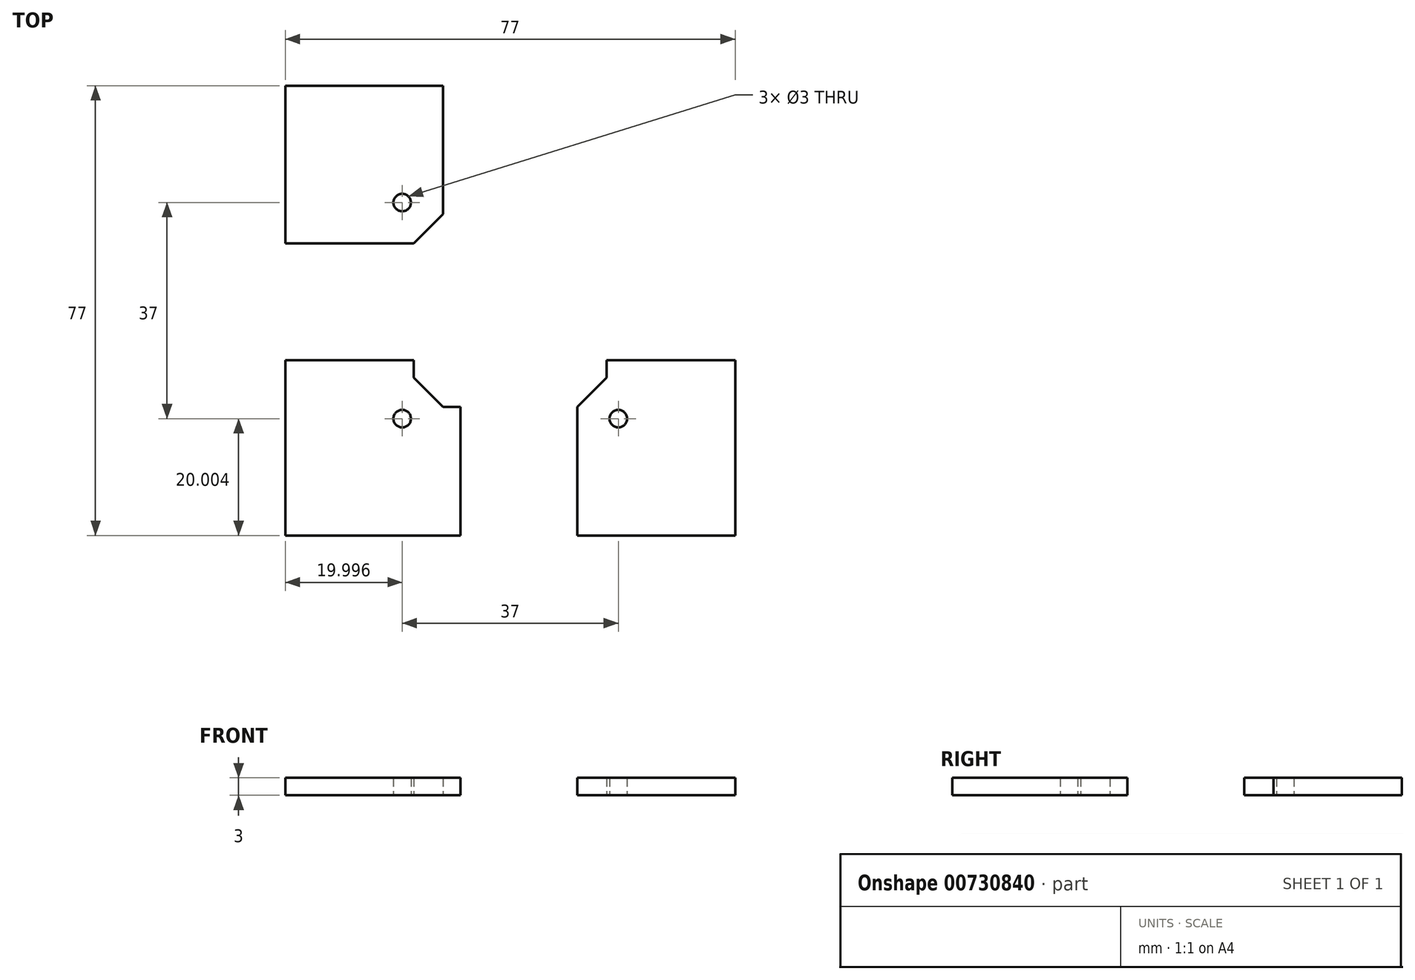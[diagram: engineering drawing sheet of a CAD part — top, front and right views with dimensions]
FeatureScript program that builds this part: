
annotation { "Feature Type Name" : "Feature", "Feature Type Description" : "" }
export const myFeature = defineFeature(function(context is Context, id is Id, definition is map)
    precondition{}
    {
        {
            var Q0;
            Q0=qCreatedBy(makeId("Top.planeOp"),FACE);
            var sketch = newSketch(context, id + "F0", { "sketchPlane" : qUnion([Q0])});
            skLineSegment(sketch, "E0.bottom", {"start": v(-24.9, 7.85) * mm, "end": v(5.1, 7.85) * mm});
            skLineSegment(sketch, "E0.top", {"start": v(-24.9, -22.15) * mm, "end": v(5.1, -22.15) * mm});
            skLineSegment(sketch, "E0.left", {"start": v(-24.9, 7.85) * mm, "end": v(-24.9, -22.15) * mm});
            skLineSegment(sketch, "E0.right", {"start": v(5.1, 7.85) * mm, "end": v(5.1, -22.15) * mm});
            skLineSegment(sketch, "E1", {"start": v(-2.9, 7.85) * mm, "end": v(-2.9, 4.85) * mm});
            skLineSegment(sketch, "E2", {"start": v(-2.9, 4.85) * mm, "end": v(2.1, -0.15) * mm});
            skLineSegment(sketch, "E3", {"start": v(2.1, -0.15) * mm, "end": v(5.1, -0.15) * mm});
            skLineSegment(sketch, "E4", {"start": v(-4.9, 7.85) * mm, "end": v(-4.9, -2.15) * mm, "construction": true});
            skCircle(sketch, "E5", {"center": v(-4.9, -2.15) * mm, "radius": 1.5 * mm});
            skLineSegment(sketch, "E6.bottom", {"start": v(-24.9, 54.85) * mm, "end": v(2.1, 54.85) * mm});
            skLineSegment(sketch, "E6.top", {"start": v(-24.9, 27.85) * mm, "end": v(2.1, 27.85) * mm});
            skLineSegment(sketch, "E6.left", {"start": v(-24.9, 54.85) * mm, "end": v(-24.9, 27.85) * mm});
            skLineSegment(sketch, "E6.right", {"start": v(2.1, 54.85) * mm, "end": v(2.1, 27.85) * mm});
            skLineSegment(sketch, "E7", {"start": v(-2.9, 27.85) * mm, "end": v(2.1, 32.85) * mm});
            skLineSegment(sketch, "E8.bottom", {"start": v(25.1, 7.85) * mm, "end": v(52.1, 7.85) * mm});
            skLineSegment(sketch, "E8.top", {"start": v(25.1, -22.15) * mm, "end": v(52.1, -22.15) * mm});
            skLineSegment(sketch, "E8.left", {"start": v(25.1, 7.85) * mm, "end": v(25.1, -22.15) * mm});
            skLineSegment(sketch, "E8.right", {"start": v(52.1, 7.85) * mm, "end": v(52.1, -22.15) * mm});
            skLineSegment(sketch, "E9", {"start": v(25.1, -0.15) * mm, "end": v(30.1, 4.85) * mm});
            skLineSegment(sketch, "E10", {"start": v(30.1, 4.85) * mm, "end": v(30.1, 7.85) * mm});
            skLineSegment(sketch, "E11", {"start": v(-24.9, 27.85) * mm, "end": v(-24.9, 7.85) * mm, "construction": true});
            skLineSegment(sketch, "E12", {"start": v(5.1, -22.15) * mm, "end": v(25.1, -22.15) * mm, "construction": true});
            skLineSegment(sketch, "E13", {"start": v(-4.9, 27.85) * mm, "end": v(-4.9, 34.85) * mm, "construction": true});
            skCircle(sketch, "E14", {"center": v(-4.9, 34.85) * mm, "radius": 1.5 * mm});
            skLineSegment(sketch, "E15", {"start": v(25.1, -2.15) * mm, "end": v(32.1, -2.15) * mm, "construction": true});
            skCircle(sketch, "E16", {"center": v(32.1, -2.15) * mm, "radius": 1.5 * mm});
            skSolve(sketch);
        }
        {
            var Q0;
            {var subQ1=sQuery(id+"F0.wireOp",EDGE,"E0.top");Q0=makeQuery(id+"F0.imprint","IMPRINT",FACE,{"disambiguationData":[TD([[makeQuery(id+"F0.imprint","IMPRINT",EDGE,{"derivedFrom":subQ1}),1.0]])]});}
            var Q1;
            {var subQ2=sQuery(id+"F0.wireOp",EDGE,"E8.top");Q1=makeQuery(id+"F0.imprint","IMPRINT",FACE,{"disambiguationData":[TD([[makeQuery(id+"F0.imprint","IMPRINT",EDGE,{"derivedFrom":subQ2}),1.0]])]});}
            var Q2;
            {var subQ1=sQuery(id+"F0.wireOp",EDGE,"E6.bottom");Q2=makeQuery(id+"F0.imprint","IMPRINT",FACE,{"disambiguationData":[TD([[makeQuery(id+"F0.imprint","IMPRINT",EDGE,{"derivedFrom":subQ1}),-1.0]])]});}
            extrude(context, id + "F1", {"entities" : qUnion([Q0, Q1, Q2]), "depth" : 3 * mm, "offsetDistance" : 25 * mm});
        }
    });
